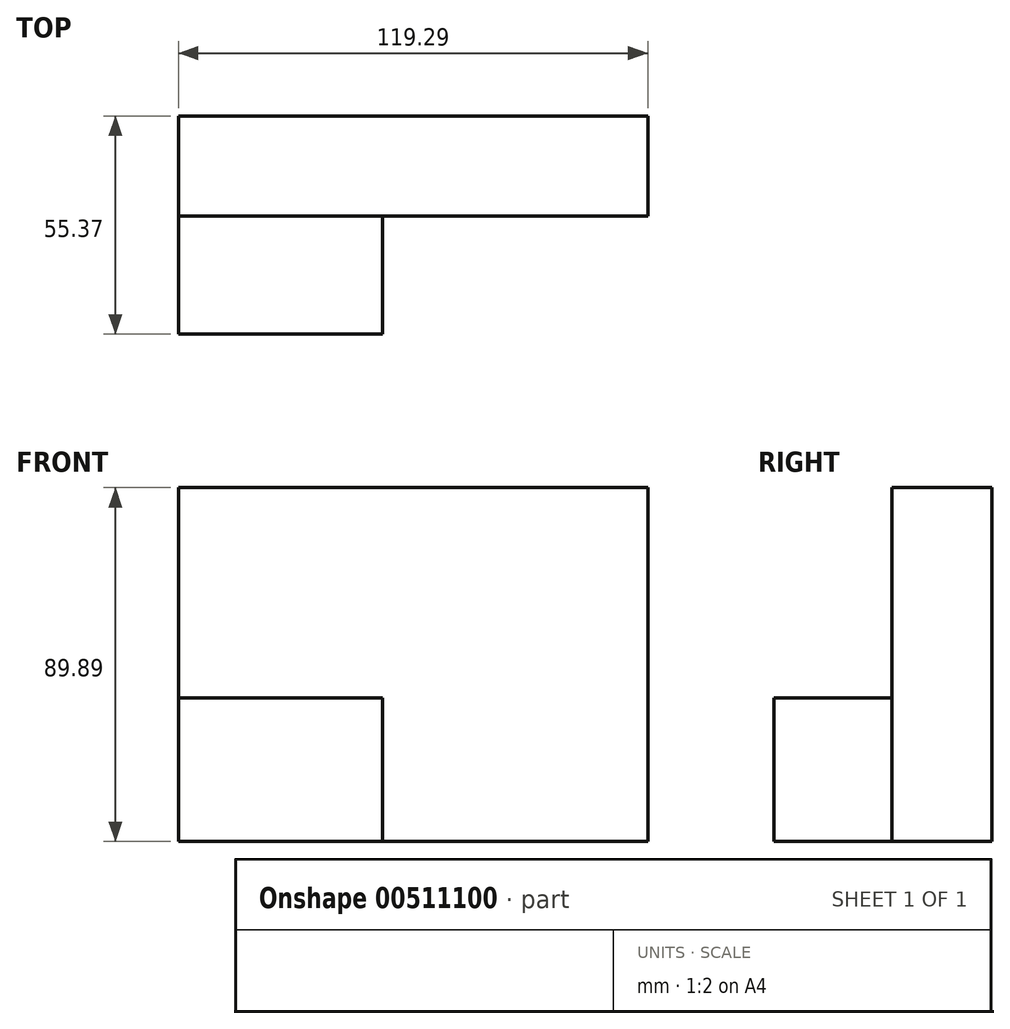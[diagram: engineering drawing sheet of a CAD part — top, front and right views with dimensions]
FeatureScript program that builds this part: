
annotation { "Feature Type Name" : "Feature", "Feature Type Description" : "" }
export const myFeature = defineFeature(function(context is Context, id is Id, definition is map)
    precondition{}
    {
        {
            var Q0;
            Q0=qCreatedBy(makeId("Front.planeOp"),FACE);
            var sketch = newSketch(context, id + "F0", { "sketchPlane" : qUnion([Q0])});
            skLineSegment(sketch, "E0.bottom", {"start": v(-58.08, 53.5) * mm, "end": v(61.21, 53.5) * mm});
            skLineSegment(sketch, "E0.top", {"start": v(-58.08, -36.4) * mm, "end": v(61.21, -36.4) * mm});
            skLineSegment(sketch, "E0.left", {"start": v(-58.08, 53.5) * mm, "end": v(-58.08, -36.4) * mm});
            skLineSegment(sketch, "E0.right", {"start": v(61.21, 53.5) * mm, "end": v(61.21, -36.4) * mm});
            skLineSegment(sketch, "E1", {"start": v(-6.27, -36.4) * mm, "end": v(-6.27, 0) * mm});
            skLineSegment(sketch, "E2", {"start": v(-6.27, 0) * mm, "end": v(-58.08, 0) * mm});
            skSolve(sketch);
        }
        {
            var Q0;
            {var subQ3=sQuery(id+"F0.wireOp",EDGE,"E1");Q0=makeQuery(id+"F0.imprint","IMPRINT",FACE,{"disambiguationData":[TD([[makeQuery(id+"F0.imprint","IMPRINT",EDGE,{"derivedFrom":subQ3}),1.0]])]});}
            extrude(context, id + "F1", {"entities" : qUnion([Q0]), "depth" : 55.37 * mm});
        }
        {
            var Q0;
            Q0 = qSketchRegion(id + "F0", true);
            extrude(context, id + "F2", {"entities" : qUnion([Q0]), "operationType" : NewBodyOperationType.ADD, "depth" : 25.4 * mm});
        }
    });
